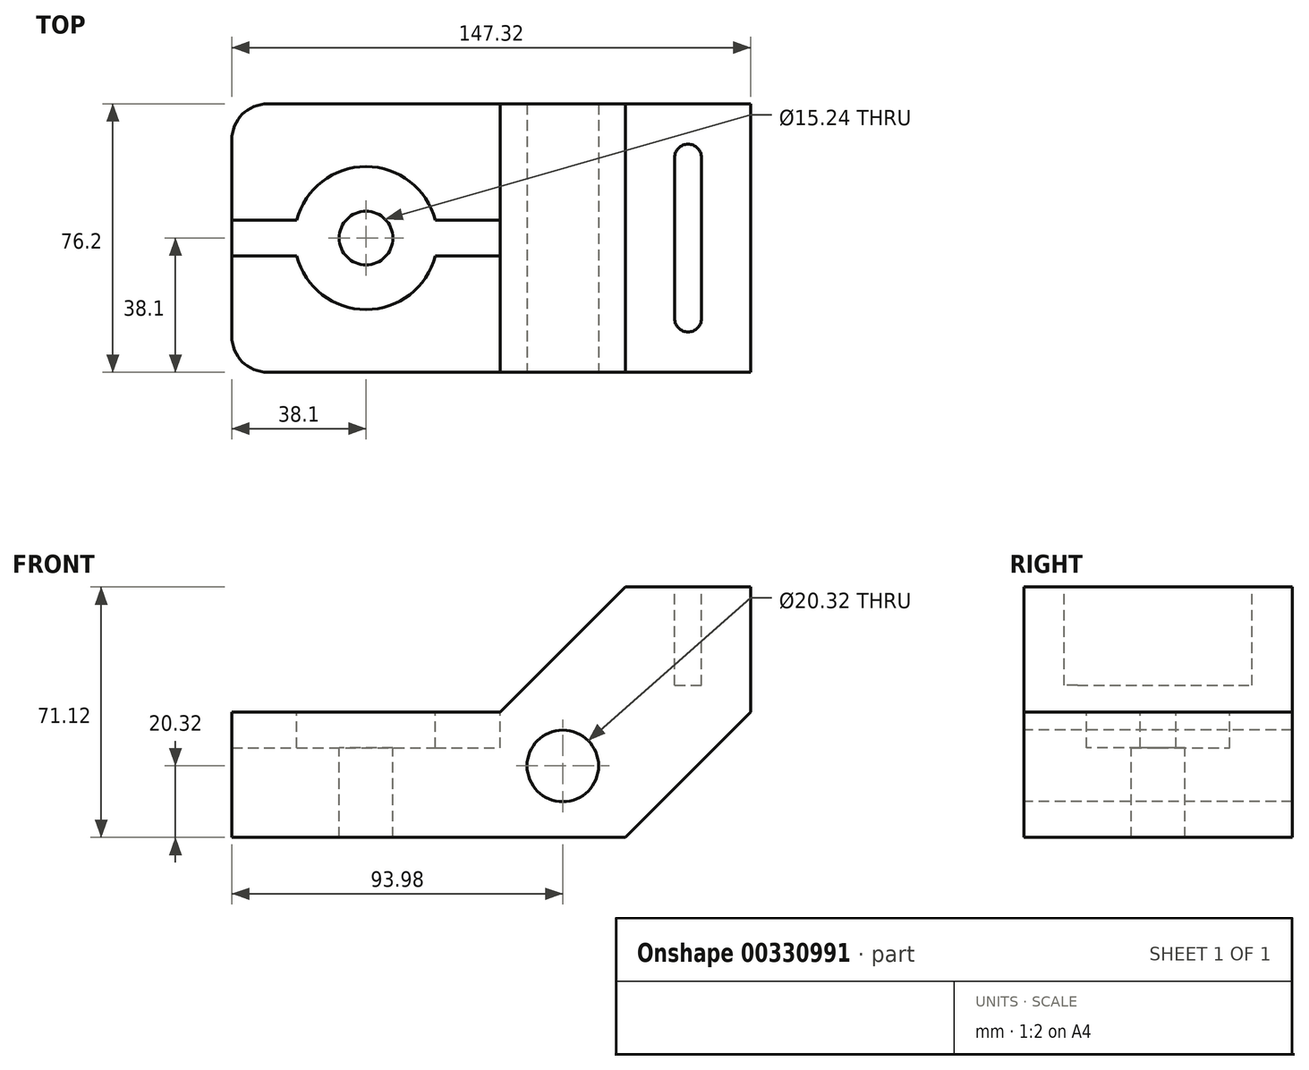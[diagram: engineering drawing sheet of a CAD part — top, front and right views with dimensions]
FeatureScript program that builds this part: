
annotation { "Feature Type Name" : "Feature", "Feature Type Description" : "" }
export const myFeature = defineFeature(function(context is Context, id is Id, definition is map)
    precondition{}
    {
        {
            var Q0;
            Q0=qCreatedBy(makeId("Front.planeOp"),FACE);
            var sketch = newSketch(context, id + "F0", { "sketchPlane" : qUnion([Q0])});
            skLineSegment(sketch, "E0", {"start": v(0, 0) * mm, "end": v(0, 35.56) * mm});
            skLineSegment(sketch, "E1", {"start": v(0, 35.56) * mm, "end": v(76.2, 35.56) * mm});
            skLineSegment(sketch, "E2", {"start": v(0, 0) * mm, "end": v(147.32, 0) * mm, "construction": true});
            skLineSegment(sketch, "E3", {"start": v(0, 0) * mm, "end": v(111.76, 0) * mm});
            skLineSegment(sketch, "E4", {"start": v(147.32, 0) * mm, "end": v(147.32, 71.12) * mm, "construction": true});
            skLineSegment(sketch, "E5", {"start": v(147.32, 71.12) * mm, "end": v(147.32, 35.56) * mm});
            skLineSegment(sketch, "E6", {"start": v(147.32, 71.12) * mm, "end": v(111.76, 71.12) * mm});
            skLineSegment(sketch, "E7", {"start": v(111.76, 71.12) * mm, "end": v(76.2, 35.56) * mm});
            skLineSegment(sketch, "E8", {"start": v(111.76, 0) * mm, "end": v(147.32, 35.56) * mm});
            skSolve(sketch);
        }
        {
            var Q0;
            Q0 = qSketchRegion(id + "F0", true);
            extrude(context, id + "F1", {"entities" : qUnion([Q0]), "oppositeDirection" : true, "depth" : 76.2 * mm});
        }
        {
            var Q0;
            Q0=makeQuery(id+"F1.opExtrude","SWEPT_FACE",FACE,{"disambiguationData":[OSD([sQuery(id+"F0.wireOp",EDGE,"E6")])]});
            var sketch = newSketch(context, id + "F2", { "sketchPlane" : qUnion([Q0])});
            skLineSegment(sketch, "E9", {"start": v(129.54, 15.24) * mm, "end": v(129.54, 60.96) * mm, "construction": true});
            skPoint(sketch, "E9.startSnap0", {"position": v(129.54, 0) * mm});
            skArc(sketch, "E10.0.startCap", {"start": v(133.35, 15.24) * mm, "mid": v(129.54, 11.43) * mm, "end": v(125.73, 15.24) * mm});
            skArc(sketch, "E10.0.endCap", {"start": v(125.73, 60.96) * mm, "mid": v(129.54, 64.77) * mm, "end": v(133.35, 60.96) * mm});
            skLineSegment(sketch, "E10.0.left", {"start": v(125.73, 15.24) * mm, "end": v(125.73, 60.96) * mm});
            skLineSegment(sketch, "E10.0.right", {"start": v(133.35, 15.24) * mm, "end": v(133.35, 60.96) * mm});
            skSolve(sketch);
        }
        {
            var Q0;
            Q0 = qSketchRegion(id + "F2", true);
            extrude(context, id + "F3", {"entities" : qUnion([Q0]), "operationType" : NewBodyOperationType.REMOVE, "oppositeDirection" : true, "depth" : 27.94 * mm});
        }
        {
            var Q0;
            Q0=makeQuery(id+"F1.opExtrude","CAP_FACE",FACE,{"disambiguationData":[OSD([sQuery(id+"F0.wireOp",EDGE,"E0"),sQuery(id+"F0.wireOp",EDGE,"E1"),sQuery(id+"F0.wireOp",EDGE,"E3"),sQuery(id+"F0.wireOp",EDGE,"E5"),sQuery(id+"F0.wireOp",EDGE,"E6"),sQuery(id+"F0.wireOp",EDGE,"E7"),sQuery(id+"F0.wireOp",EDGE,"E8")])],"isStart":true});
            var sketch = newSketch(context, id + "F4", { "sketchPlane" : qUnion([Q0])});
            skPoint(sketch, "E11", {"position": v(93.98, 20.32) * mm});
            skCircle(sketch, "E12", {"center": v(93.98, 20.32) * mm, "radius": 10.16 * mm});
            skSolve(sketch);
        }
        {
            var Q0;
            Q0 = qSketchRegion(id + "F4", true);
            extrude(context, id + "F5", {"entities" : qUnion([Q0]), "operationType" : NewBodyOperationType.REMOVE, "endBound" : BoundingType.THROUGH_ALL, "oppositeDirection" : true, "depth" : 25.4 * mm});
        }
        {
            var Q0;
            Q0=makeQuery(id+"F1.opExtrude","SWEPT_FACE",FACE,{"disambiguationData":[OSD([sQuery(id+"F0.wireOp",EDGE,"E1")])]});
            var sketch = newSketch(context, id + "F6", { "sketchPlane" : qUnion([Q0])});
            skLineSegment(sketch, "E13", {"start": v(0, 38.1) * mm, "end": v(76.2, 38.1) * mm, "construction": true});
            skPoint(sketch, "E14", {"position": v(38.1, 38.1) * mm});
            skLineSegment(sketch, "E15", {"start": v(0, 43.18) * mm, "end": v(0, 33.02) * mm});
            skCircle(sketch, "E16", {"center": v(38.1, 38.1) * mm, "radius": 7.62 * mm});
            skCircle(sketch, "E17", {"center": v(38.1, 38.1) * mm, "radius": 20.32 * mm});
            skLineSegment(sketch, "E18", {"start": v(0, 43.18) * mm, "end": v(18.43, 43.18) * mm});
            skLineSegment(sketch, "E19", {"start": v(0, 33.02) * mm, "end": v(18.43, 33.02) * mm});
            skLineSegment(sketch, "E20", {"start": v(57.77, 43.18) * mm, "end": v(76.2, 43.18) * mm});
            skLineSegment(sketch, "E21", {"start": v(57.77, 33.02) * mm, "end": v(76.2, 33.02) * mm});
            skLineSegment(sketch, "E22", {"start": v(76.2, 33.02) * mm, "end": v(76.2, 43.18) * mm});
            skSolve(sketch);
        }
        {
            var Q0;
            Q0=sQuery(id+"F6.wireOp",VERTEX,"E14");
            var Q1;
            Q1=makeQuery(id+"F1.opExtrude","SWEPT_BODY",BODY,{"disambiguationData":[OSD([sQuery(id+"F0.wireOp",EDGE,"E0"),sQuery(id+"F0.wireOp",EDGE,"E1"),sQuery(id+"F0.wireOp",EDGE,"E3"),sQuery(id+"F0.wireOp",EDGE,"E5"),sQuery(id+"F0.wireOp",EDGE,"E6"),sQuery(id+"F0.wireOp",EDGE,"E7"),sQuery(id+"F0.wireOp",EDGE,"E8")])]});
            hole(context, id + "F7", {"style" : HoleStyle.C_BORE, "endStyle" : HoleEndStyle.THROUGH, "holeDiameter" : 15.24 * mm, "cBoreDiameter" : 40.64 * mm, "cBoreDepth" : 10.16 * mm, "tappedDepth" : 12.7 * mm, "tapClearance" : 3, "locations" : qUnion([Q0]), "scope" : qUnion([Q1])});
        }
        {
            var Q0;
            Q0=makeQuery(id+"F6.imprint","IMPRINT",FACE,{"disambiguationData":[TD([[makeQuery(id+"F6.imprint","IMPRINT",EDGE,{"derivedFrom":sQuery(id+"F6.wireOp",EDGE,"E15")}),1.0]])]});
            var Q1;
            {var subQ0=sQuery(id+"F6.wireOp",EDGE,"E20");Q1=makeQuery(id+"F6.imprint","IMPRINT",FACE,{"disambiguationData":[TD([[makeQuery(id+"F6.imprint","IMPRINT",EDGE,{"derivedFrom":subQ0}),-1.0]])]});}
            extrude(context, id + "F8", {"entities" : qUnion([Q0, Q1]), "operationType" : NewBodyOperationType.REMOVE, "oppositeDirection" : true, "depth" : 10.16 * mm});
        }
        {
            var Q0;
            Q0=makeQuery(id+"F1.opExtrude","CAP_EDGE",EDGE,{"disambiguationData":[OSD([sQuery(id+"F0.wireOp",EDGE,"E0")])],"isStart":false});
            var Q1;
            Q1=makeQuery(id+"F1.opExtrude","CAP_EDGE",EDGE,{"disambiguationData":[OSD([sQuery(id+"F0.wireOp",EDGE,"E0")])],"isStart":true});
            fillet(context, id + "F9", {"entities" : qUnion([Q0, Q1]), "radius" : 10.16 * mm, "tangentPropagation" : true, "allowEdgeOverflow" : false});
        }
    });
